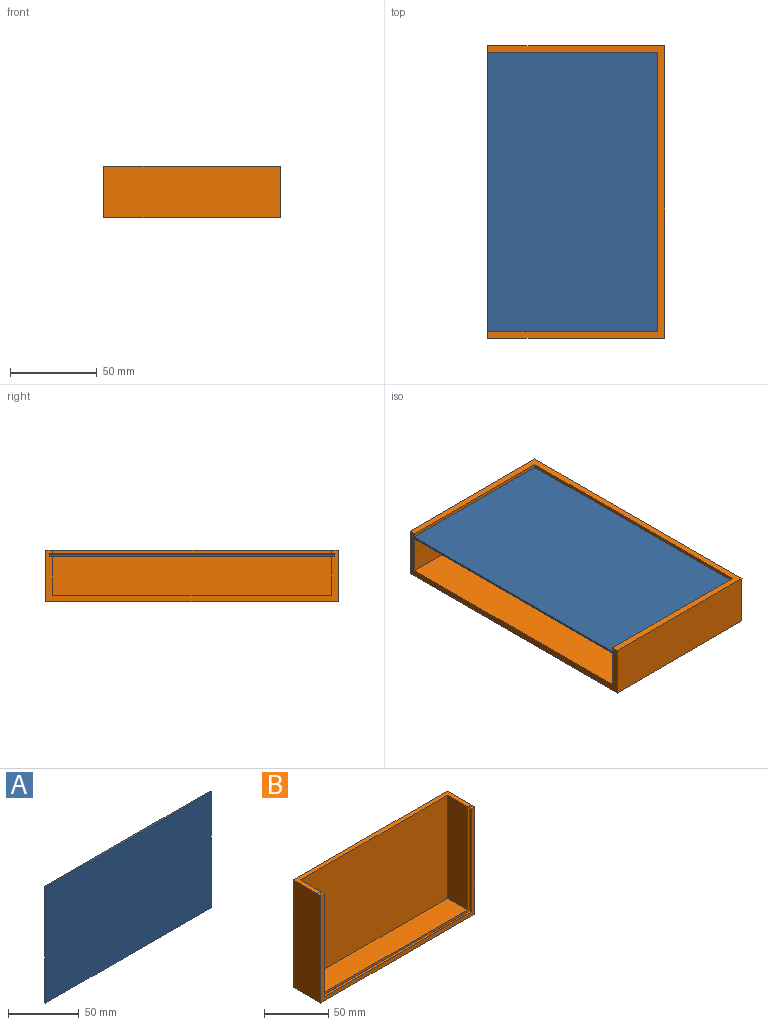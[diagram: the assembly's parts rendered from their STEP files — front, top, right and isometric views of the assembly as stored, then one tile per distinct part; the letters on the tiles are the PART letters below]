
ASSEMBLY  parts=2 mates=1
PART A: 6 faces, bbox 165x1.2x100 mm
  f0: plane 100x1.2mm, normal (1,0,0), area 120mm2, adj f1,f3,f4,f5
  f1: plane 165x1.2mm, normal (0,0,1), area 198mm2, adj f0,f2,f4,f5
  f2: plane 100x1.2mm, normal (-1,0,0), area 120mm2, adj f1,f3,f4,f5
  f3: plane 165x1.2mm, normal (0,0,-1), area 198mm2, adj f0,f2,f4,f5
  f4: plane 165x100mm, normal (0,-1,0), area 16500mm2, adj f0,f1,f2,f3
  f5: plane 165x100mm, normal (0,1,0), area 16500mm2, adj f0,f1,f2,f3
PART B: 18 faces, bbox 169x30x102 mm
  f0: plane 98x22mm, normal (1,0,0), area 2156mm2, adj f1,f4,f12,f13
  f1: plane 161x22mm, normal (0,0,1), area 3542mm2, adj f0,f2,f12,f13
  f2: plane 98x22mm, normal (-1,0,0), area 2156mm2, adj f1,f4,f12,f13
  f3: plane 169x102mm, normal (0,-1,0), area 1460mm2, adj f4,f5,f6,f7,f9,f10,f11
  f4: plane 169x30mm, normal (0,0,1), area 876mm2, adj f0,f2,f3,f5,f7,f8,f9,f11
  f5: plane 102x30mm, normal (-1,0,0), area 3060mm2, adj f3,f4,f6,f8
  f6: plane 169x30mm, normal (0,0,-1), area 5070mm2, adj f3,f5,f7,f8
  f7: plane 102x30mm, normal (1,0,0), area 3060mm2, adj f3,f4,f6,f8
  f8: plane 169x102mm, normal (0,1,0), area 17238mm2, adj f4,f5,f6,f7
  f9: plane 98x2mm, normal (1,0,0), area 196mm2, adj f3,f4,f10,f15
  f10: plane 161x2mm, normal (0,0,1), area 322mm2, adj f3,f9,f11,f15
  f11: plane 98x2mm, normal (-1,0,0), area 196mm2, adj f3,f4,f10,f15
  f12: plane 161x98mm, normal (0,-1,0), area 15778mm2, adj f0,f1,f2,f4
  f13: plane 165x100mm, normal (0,-1,0), area 722mm2, adj f0,f1,f2,f4,f14,f16,f17
  f14: plane 100x2mm, normal (1,0,0), area 200mm2, adj f4,f13,f15,f17
  f15: plane 165x100mm, normal (0,1,0), area 722mm2, adj f4,f9,f10,f11,f14,f16,f17
  f16: plane 100x2mm, normal (-1,0,0), area 200mm2, adj f4,f13,f15,f17
  f17: plane 165x2mm, normal (0,0,1), area 330mm2, adj f13,f14,f15,f16
PLACE A rot(axis=(0.58,0.58,0.58),120deg) t=(174.31,-53.58,31.29)mm
PLACE B rot(axis=(-0.58,-0.58,0.58),120deg) t=(174.54,-53.58,33.69)mm
MATE slider A.f1 <-> B.f17  axis (1,0,0) through (224.31,-136.08,30.69)mm
